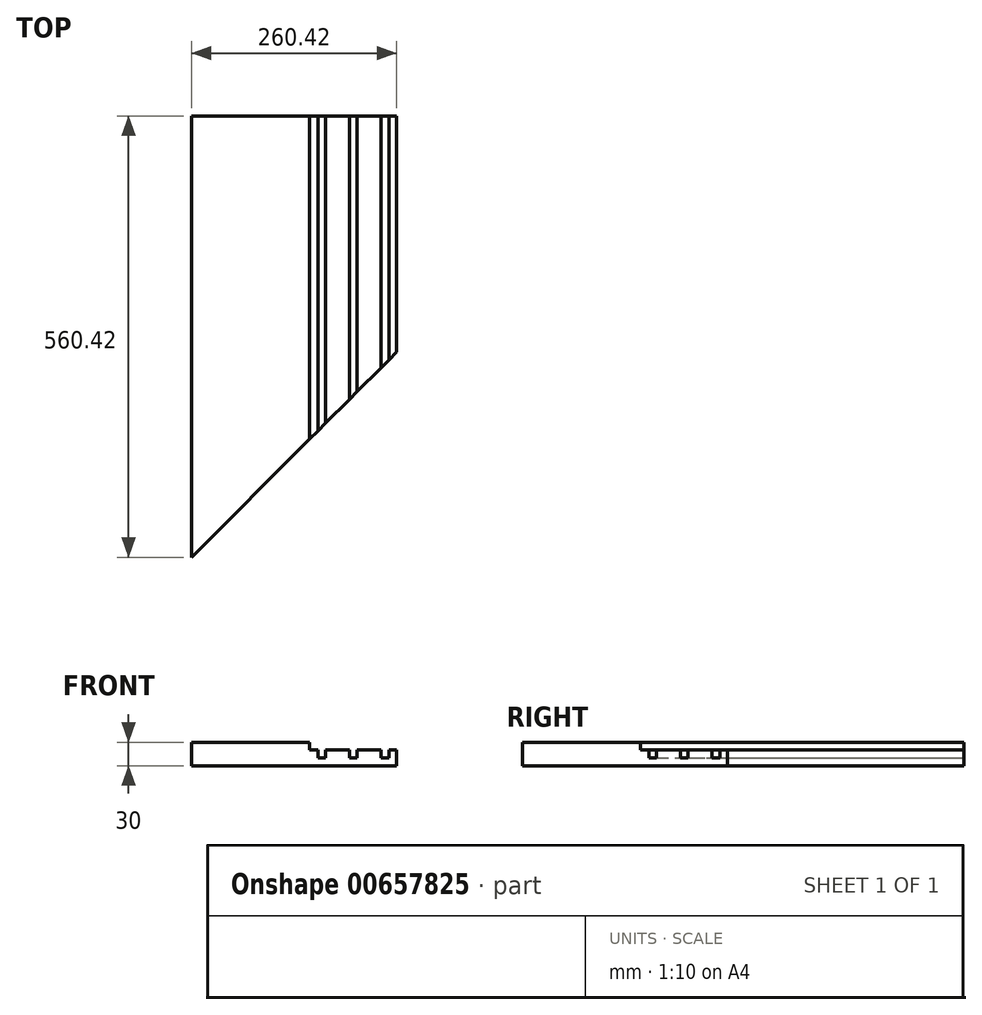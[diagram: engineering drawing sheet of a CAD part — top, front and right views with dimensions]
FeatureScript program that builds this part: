
annotation { "Feature Type Name" : "Feature", "Feature Type Description" : "" }
export const myFeature = defineFeature(function(context is Context, id is Id, definition is map)
    precondition{}
    {
        {
            var Q0;
            Q0=qCreatedBy(makeId("Front.planeOp"),FACE);
            var sketch = newSketch(context, id + "F0", { "sketchPlane" : qUnion([Q0])});
            skLineSegment(sketch, "E0.bottom", {"start": v(-41.87, -7.44) * mm, "end": v(-191.87, -7.44) * mm});
            skLineSegment(sketch, "E0.top", {"start": v(-41.87, -37.44) * mm, "end": v(-191.87, -37.44) * mm});
            skLineSegment(sketch, "E0.left", {"start": v(-41.87, -7.44) * mm, "end": v(-41.87, -37.44) * mm});
            skLineSegment(sketch, "E0.right", {"start": v(-191.87, -7.44) * mm, "end": v(-191.87, -37.44) * mm});
            skLineSegment(sketch, "E1.bottom", {"start": v(-41.87, -37.44) * mm, "end": v(58.55, -37.44) * mm});
            skLineSegment(sketch, "E1.top", {"start": v(-41.87, -27.44) * mm, "end": v(58.55, -27.44) * mm});
            skLineSegment(sketch, "E1.left", {"start": v(-41.87, -37.44) * mm, "end": v(-41.87, -27.44) * mm});
            skLineSegment(sketch, "E1.right", {"start": v(58.55, -37.44) * mm, "end": v(58.55, -27.44) * mm});
            skLineSegment(sketch, "E2.bottom", {"start": v(-41.87, -27.44) * mm, "end": v(-31.53, -27.44) * mm});
            skLineSegment(sketch, "E2.top", {"start": v(-41.87, -17.44) * mm, "end": v(-31.53, -17.44) * mm});
            skLineSegment(sketch, "E2.left", {"start": v(-41.87, -27.44) * mm, "end": v(-41.87, -17.44) * mm});
            skLineSegment(sketch, "E2.right", {"start": v(-31.53, -27.44) * mm, "end": v(-31.53, -17.44) * mm});
            skLineSegment(sketch, "E3", {"start": v(-31.53, -27.44) * mm, "end": v(-21.53, -27.44) * mm});
            skLineSegment(sketch, "E4.bottom", {"start": v(-21.53, -27.44) * mm, "end": v(8.47, -27.44) * mm});
            skLineSegment(sketch, "E4.top", {"start": v(-21.53, -17.44) * mm, "end": v(8.47, -17.44) * mm});
            skLineSegment(sketch, "E4.left", {"start": v(-21.53, -27.44) * mm, "end": v(-21.53, -17.44) * mm});
            skLineSegment(sketch, "E4.right", {"start": v(8.47, -27.44) * mm, "end": v(8.47, -17.44) * mm});
            skLineSegment(sketch, "E5", {"start": v(8.47, -27.44) * mm, "end": v(18.47, -27.44) * mm});
            skLineSegment(sketch, "E6.bottom", {"start": v(18.47, -27.44) * mm, "end": v(48.47, -27.44) * mm});
            skLineSegment(sketch, "E6.top", {"start": v(18.47, -17.44) * mm, "end": v(48.47, -17.44) * mm});
            skLineSegment(sketch, "E6.left", {"start": v(18.47, -27.44) * mm, "end": v(18.47, -17.44) * mm});
            skLineSegment(sketch, "E6.right", {"start": v(48.47, -27.44) * mm, "end": v(48.47, -17.44) * mm});
            skLineSegment(sketch, "E7.bottom", {"start": v(58.55, -37.44) * mm, "end": v(68.55, -37.44) * mm});
            skLineSegment(sketch, "E7.top", {"start": v(58.55, -17.44) * mm, "end": v(68.55, -17.44) * mm});
            skLineSegment(sketch, "E7.left", {"start": v(58.55, -37.44) * mm, "end": v(58.55, -17.44) * mm});
            skLineSegment(sketch, "E7.right", {"start": v(68.55, -37.44) * mm, "end": v(68.55, -17.44) * mm});
            skSolve(sketch);
        }
        {
            var Q0;
            {var subQ1=sQuery(id+"F0.wireOp",EDGE,"E1.right");var subQ2=makeQuery(id+"F0.imprint","IMPRINT",EDGE,{"derivedFrom":subQ1});var subQ14=sQuery(id+"F0.wireOp",EDGE,"E1.bottom");var subQ22=sQuery(id+"F0.wireOp",EDGE,"E2.top");var subQ25=sQuery(id+"F0.wireOp",EDGE,"E0.bottom");Q0=qUnion([makeQuery(id+"F0.imprint","IMPRINT",FACE,{"disambiguationData":[TD([[makeQuery(id+"F0.imprint","IMPRINT",EDGE,{"derivedFrom":subQ25}),1.0]])]}),makeQuery(id+"F0.imprint","IMPRINT",FACE,{"disambiguationData":[TD([[makeQuery(id+"F0.imprint","IMPRINT",EDGE,{"derivedFrom":sQuery(id+"F0.wireOp",EDGE,"E6.top")}),-1.0]])]}),makeQuery(id+"F0.imprint","IMPRINT",FACE,{"disambiguationData":[TD([[makeQuery(id+"F0.imprint","IMPRINT",EDGE,{"derivedFrom":subQ22}),-1.0]])]}),makeQuery(id+"F0.imprint","IMPRINT",FACE,{"disambiguationData":[TD([[makeQuery(id+"F0.imprint","IMPRINT",EDGE,{"derivedFrom":sQuery(id+"F0.wireOp",EDGE,"E4.top")}),-1.0]])]}),makeQuery(id+"F0.imprint","IMPRINT",FACE,{"disambiguationData":[TD([[makeQuery(id+"F0.imprint","IMPRINT",EDGE,{"derivedFrom":subQ14}),1.0]])]}),makeQuery(id+"F0.imprint","IMPRINT",FACE,{"disambiguationData":[TD([[subQ2,-1.0]])]})]);}
            extrude(context, id + "F1", {"entities" : qUnion([Q0]), "endBound" : BoundingType.SYMMETRIC, "depth" : 600 * mm, "offsetDistance" : 25 * mm});
        }
        {
            var Q0;
            Q0=makeQuery(id+"F1.opExtrude","CAP_EDGE",EDGE,{"disambiguationData":[OSD([sQuery(id+"F0.wireOp",EDGE,"E7.right")])],"isStart":false});
            chamfer(context, id + "F2", {"entities" : qUnion([Q0]), "width" : 300 * mm, "tangentPropagation" : true});
        }
    });
